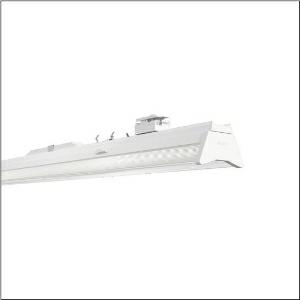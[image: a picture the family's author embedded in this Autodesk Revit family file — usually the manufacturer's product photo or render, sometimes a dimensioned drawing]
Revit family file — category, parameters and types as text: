
# Revit family: licross_11_performance_mo_51td16mn4axg
name_source: partatom
category: Lighting Fixtures
units: mm (PartAtom-declared; Revit-internal decimal feet)

## family parameters
Cut with Voids When Loaded = No
Host = Face
Light Source = No
Part Type = Normal
Room Calculation Point = No
Round Connector Dimension = Use Diameter
Shared = No

## types (1)
- --- (1 x LED, 10160 lm, 55.3 W, 4000K)
    Apparent Load = 55 VA
    CIE Flux Codes = 66 88 96 79 100
    Color Rendering = 80
    Color Temperature = 4000K
    Default Elevation = 1800 mm
    Description = Licross 11 Performance MO, luminaire insert, of sheet steel, galvanised, coil coated, white, length: 1.500mm, width: 120mm, height: 123mm, LED rated luminous flux: 10.160lm, light colour: 840, SDCM (Standard Deviation of Colour Matching)MacAdam ≤ 2 SDCM (initial), control gear: ON/OFF Multilumen, with plug, 3-pole, with phase selection, mains connection: 220..240V, AC, 50/60Hz, rated input power: 55W, internal wiring halogen-free, primary light control with lens, of plastic, primary optical cover: cover, of PMMA, light emission: direct/indirect distribution, primary light characteristic: symmetric, protection rating (complete): IP54, insulation class (complete): insulation class I (protective earthing), certification: CE, ENEC, VDE, UKCA, protection symbol: D if used in an environment with non-conductive dust loads with corresponding accessories, impact resistance: IK06, permissible ambient temperature for indoor applications: -35..+40°C, corresponds to IFS (International Featured Standards) requirements for safety and quality in the food industry, reducing of maximum allowable ambient temperature of 5°C with ceiling mounting, LABS conformity tested according to VDMA 24364:2018-05, The light source and the operating device comply with the requirements of the Ecodesign Regulation (EU) 2019/2020 and are replaceable in accordance with this regulation, packaging unit: 1 piece
    Height = 114 mm
    Lamp = 1 x LED
    Lamp Light Flux = 10160 lm
    Lamp Power = 55.3 W
    Lamp count = 1
    Length = 1500 mm
    Luminous efficacy = 184 lm/W
    Manufacturer = Siteco
    ModVariant = No
    Model = 51TD16MN4AXG
    Mounting Place = Ceiling
    Mounting Type = Pendant
    Number of Poles = 1
    OnlyDefault = Yes
    Power Factor = 1
    Product Name = Licross 11 Performance MO
    Product group = luminaire insert | ceiling pendant
    ProductGroupID = 901
    Protection Class = Protection class I
    Protection Degree = IP 54
    RLX_Detail_Level = 1
    RLX_Emergency_Light_Flux = 0 lm
    RLX_Emergency_Type = 0
    RLX_Emergency_Type_DB = No
    RlxData = <blob elided: 32081 chars, md5=c9b001ca>
    Socket = socket
    Standby Power = 0 W
    System Light Flux = 10160 lm
    System Power = 55 W
    Type Comments = factory setting: luminous flux: 100 % | (A | C | E) | 126 mA
    Type Image = l_1256138.jpg
    URL = http://relux.com
    VarID = @adj_090557
    Voltage = 0 V
    Weight = 0.00 kg
    Width = 120 mm

## geometry (parser evidence)
native form markers: Blend x4, Sweep x11
no freeform markers — native parametric forms only
